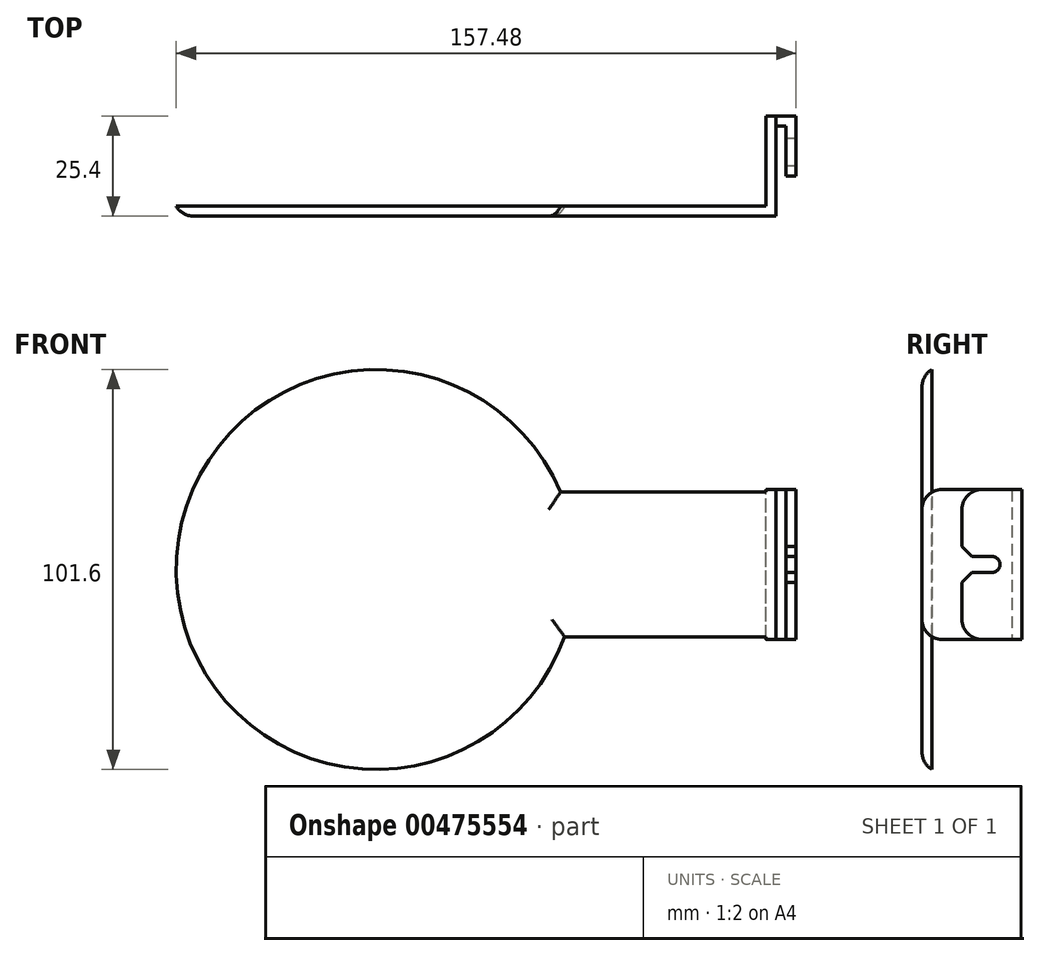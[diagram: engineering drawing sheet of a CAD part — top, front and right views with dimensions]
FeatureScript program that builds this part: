
annotation { "Feature Type Name" : "Feature", "Feature Type Description" : "" }
export const myFeature = defineFeature(function(context is Context, id is Id, definition is map)
    precondition{}
    {
        {
            var Q0;
            Q0=qCreatedBy(makeId("Front.planeOp"),FACE);
            var sketch = newSketch(context, id + "F0", { "sketchPlane" : qUnion([Q0])});
            skLineSegment(sketch, "E0", {"start": v(-38.46, -17.77) * mm, "end": v(63.14, -17.77) * mm});
            skLineSegment(sketch, "E1", {"start": v(63.14, -17.77) * mm, "end": v(63.14, 20.33) * mm});
            skLineSegment(sketch, "E2", {"start": v(63.14, 20.33) * mm, "end": v(-38.46, 20.33) * mm});
            skLineSegment(sketch, "E3", {"start": v(-38.46, 20.33) * mm, "end": v(-38.46, -17.77) * mm});
            skPoint(sketch, "E4", {"position": v(12.34, -17.77) * mm});
            skPoint(sketch, "E5", {"position": v(12.34, 20.33) * mm});
            skLineSegment(sketch, "E6", {"start": v(12.34, 20.33) * mm, "end": v(12.34, -17.77) * mm, "construction": true});
            skPoint(sketch, "E7", {"position": v(-38.46, 0) * mm});
            skCircle(sketch, "E8", {"center": v(-38.46, 0) * mm, "radius": 50.8 * mm});
            skSolve(sketch);
        }
        {
            var Q0;
            {var subQ0=sQuery(id+"F0.wireOp",EDGE,"E3");Q0=makeQuery(id+"F0.imprint","IMPRINT",FACE,{"disambiguationData":[TD([[makeQuery(id+"F0.imprint","IMPRINT",EDGE,{"derivedFrom":subQ0}),-1.0]])]});}
            var Q1;
            {var subQ0=sQuery(id+"F0.wireOp",EDGE,"E1");Q1=makeQuery(id+"F0.imprint","IMPRINT",FACE,{"disambiguationData":[TD([[makeQuery(id+"F0.imprint","IMPRINT",EDGE,{"derivedFrom":subQ0}),1.0]])]});}
            var Q2;
            {var subQ0=sQuery(id+"F0.wireOp",EDGE,"E3");Q2=makeQuery(id+"F0.imprint","IMPRINT",FACE,{"disambiguationData":[TD([[makeQuery(id+"F0.imprint","IMPRINT",EDGE,{"derivedFrom":subQ0}),1.0]])]});}
            extrude(context, id + "F1", {"entities" : qUnion([Q0, Q1, Q2]), "depth" : 2.54 * mm});
        }
        {
            var Q0;
            Q0=makeQuery(id+"F1.opExtrude","SWEPT_FACE",FACE,{"disambiguationData":[OSD([sQuery(id+"F0.wireOp",EDGE,"E1")])]});
            var sketch = newSketch(context, id + "F2", { "sketchPlane" : qUnion([Q0])});
            skLineSegment(sketch, "E9", {"start": v(-2.54, -17.77) * mm, "end": v(22.86, -17.77) * mm});
            skLineSegment(sketch, "E10", {"start": v(22.86, -17.77) * mm, "end": v(22.86, 20.33) * mm});
            skLineSegment(sketch, "E11", {"start": v(22.86, 20.33) * mm, "end": v(-2.54, 20.33) * mm});
            skLineSegment(sketch, "E12", {"start": v(-2.54, 20.33) * mm, "end": v(-2.54, -17.77) * mm});
            skSolve(sketch);
        }
        {
            var Q0;
            {var subQ2=sQuery(id+"F2.wireOp",EDGE,"E10");Q0=makeQuery(id+"F2.imprint","IMPRINT",FACE,{"disambiguationData":[TD([[makeQuery(id+"F2.imprint","IMPRINT",EDGE,{"derivedFrom":subQ2}),1.0]])]});}
            extrude(context, id + "F3", {"entities" : qUnion([Q0]), "operationType" : NewBodyOperationType.ADD, "oppositeDirection" : true, "depth" : 2.54 * mm});
        }
        {
            var Q0;
            Q0=makeQuery(id+"F3.opExtrude","SWEPT_FACE",FACE,{"disambiguationData":[OSD([sQuery(id+"F2.wireOp",EDGE,"E10")])]});
            var sketch = newSketch(context, id + "F4", { "sketchPlane" : qUnion([Q0])});
            skLineSegment(sketch, "E13", {"start": v(-60.6, 20.33) * mm, "end": v(-60.6, -17.77) * mm});
            skLineSegment(sketch, "E14", {"start": v(-60.6, -17.77) * mm, "end": v(-68.22, -17.77) * mm});
            skLineSegment(sketch, "E15", {"start": v(-68.22, -17.77) * mm, "end": v(-68.22, 20.33) * mm});
            skLineSegment(sketch, "E16", {"start": v(-68.22, 20.33) * mm, "end": v(-60.6, 20.33) * mm});
            skSolve(sketch);
        }
        {
            var Q0;
            {var subQ2=sQuery(id+"F4.wireOp",EDGE,"E15");Q0=makeQuery(id+"F4.imprint","IMPRINT",FACE,{"disambiguationData":[TD([[makeQuery(id+"F4.imprint","IMPRINT",EDGE,{"derivedFrom":subQ2}),-1.0]])]});}
            extrude(context, id + "F5", {"entities" : qUnion([Q0]), "oppositeDirection" : true, "depth" : 2.54 * mm});
        }
        {
            var Q0;
            Q0=makeQuery(id+"F5.opExtrude","SWEPT_FACE",FACE,{"disambiguationData":[OSD([sQuery(id+"F4.wireOp",EDGE,"E15")])]});
            var sketch = newSketch(context, id + "F6", { "sketchPlane" : qUnion([Q0])});
            skLineSegment(sketch, "E17", {"start": v(22.86, 20.33) * mm, "end": v(7.62, 20.33) * mm});
            skLineSegment(sketch, "E18", {"start": v(7.62, 20.33) * mm, "end": v(7.62, -17.77) * mm});
            skLineSegment(sketch, "E19", {"start": v(7.62, -17.77) * mm, "end": v(22.86, -17.77) * mm});
            skLineSegment(sketch, "E20", {"start": v(22.86, -17.77) * mm, "end": v(22.86, 20.33) * mm});
            skPoint(sketch, "E21", {"position": v(7.62, 1.28) * mm});
            skCircle(sketch, "E22", {"center": v(15.24, 1.28) * mm, "radius": 2.03 * mm});
            skLineSegment(sketch, "E23", {"start": v(15.24, 3.3) * mm, "end": v(7.62, 3.3) * mm});
            skLineSegment(sketch, "E24", {"start": v(7.62, 1.28) * mm, "end": v(15.24, 1.28) * mm, "construction": true});
            skLineSegment(sketch, "E25.MirrorCS", {"start": v(15.24, -0.76) * mm, "end": v(7.62, -0.76) * mm});
            skLineSegment(sketch, "E26", {"start": v(15.24, 3.3) * mm, "end": v(15.24, -0.76) * mm, "construction": true});
            skSolve(sketch);
        }
        {
            var Q0;
            {var subQ8=sQuery(id+"F6.wireOp",EDGE,"4G0HyOGl-Q5EW-GZG8-jg59-l8MfHQK35u7S");Q0=makeQuery(id+"F6.imprint","IMPRINT",FACE,{"disambiguationData":[TD([[makeQuery(id+"F6.imprint","IMPRINT",EDGE,{"derivedFrom":subQ8}),-1.0]])]});}
            var Q1;
            {var subQ0=sQuery(id+"F6.wireOp",EDGE,"E20");Q1=makeQuery(id+"F6.imprint","IMPRINT",FACE,{"disambiguationData":[TD([[makeQuery(id+"F6.imprint","IMPRINT",EDGE,{"derivedFrom":subQ0}),1.0]])]});}
            var Q2;
            {var subQ6=sQuery(id+"F6.wireOp",EDGE,"E23");Q2=makeQuery(id+"F6.imprint","IMPRINT",FACE,{"disambiguationData":[TD([[makeQuery(id+"F6.imprint","IMPRINT",EDGE,{"derivedFrom":subQ6}),-1.0]])]});}
            var Q3;
            {var subQ0=sQuery(id+"F6.wireOp",EDGE,"E19");var subQ1=sQuery(id+"F6.wireOp",EDGE,"E18");var subQ2=makeQuery(id+"F6.imprint","INTERSECT",VERTEX,{"derivedFrom":[subQ1,subQ0]});Q3=makeQuery(id+"F6.imprint","IMPRINT",FACE,{"disambiguationData":[TD([[makeQuery(id+"F6.imprint","IMPRINT",EDGE,{"disambiguationData":[TD([[subQ2,1.0]])],"derivedFrom":subQ1}),1.0]])]});}
            extrude(context, id + "F7", {"entities" : qUnion([Q0, Q1, Q2, Q3]), "operationType" : NewBodyOperationType.ADD, "oppositeDirection" : true, "depth" : 2.54 * mm, "offsetDistance" : 25.4 * mm});
        }
        {
            var Q0;
            Q0=makeQuery(id+"F1.opExtrude","CAP_EDGE",EDGE,{"disambiguationData":[OSD([sQuery(id+"F0.wireOp",EDGE,"E8")])],"isStart":false});
            var Q1;
            Q1=makeQuery(id+"F1.opExtrude","CAP_EDGE",EDGE,{"disambiguationData":[OSD([sQuery(id+"F0.wireOp",EDGE,"E2")])],"isStart":false});
            var Q2;
            Q2=makeQuery(id+"F1.opExtrude","CAP_EDGE",EDGE,{"disambiguationData":[OSD([sQuery(id+"F0.wireOp",EDGE,"E0")])],"isStart":false});
            fillet(context, id + "F8", {"entities" : qUnion([Q0, Q1, Q2]), "radius" : 5.08 * mm, "tangentPropagation" : true, "allowEdgeOverflow" : false});
        }
        {
            var Q0;
            Q0=makeQuery(id+"F7.opExtrude","SWEPT_EDGE",EDGE,{"disambiguationData":[OSD([sQuery(id+"F6.wireOp",EDGE,"E18"),sQuery(id+"F6.wireOp",EDGE,"E19")])]});
            var Q1;
            Q1=makeQuery(id+"F7.opExtrude","SWEPT_EDGE",EDGE,{"disambiguationData":[OSD([sQuery(id+"F6.wireOp",EDGE,"E17"),sQuery(id+"F6.wireOp",EDGE,"E18")])]});
            fillet(context, id + "F9", {"entities" : qUnion([Q0, Q1]), "radius" : 5.08 * mm, "tangentPropagation" : true, "allowEdgeOverflow" : false});
        }
        {
            var Q0;
            Q0=makeQuery(id+"F7.opExtrude","SWEPT_EDGE",EDGE,{"disambiguationData":[OSD([sQuery(id+"F6.wireOp",EDGE,"E18"),sQuery(id+"F6.wireOp",EDGE,"E23")])]});
            var Q1;
            Q1=makeQuery(id+"F7.opExtrude","SWEPT_EDGE",EDGE,{"disambiguationData":[OSD([sQuery(id+"F6.wireOp",EDGE,"E18"),sQuery(id+"F6.wireOp",EDGE,"E25.MirrorCS")])]});
            chamfer(context, id + "F10", {"entities" : qUnion([Q0, Q1]), "width" : 2.54 * mm, "tangentPropagation" : true});
        }
    });
